# Revit family: Sanitary_Shower-Trays_Sanindusa_Marina-Shower-Tray-With-Schist-Texture-Surface
name_source: partatom
category: Plumbing Fixtures
revit_build: Autodesk Revit 2018 (Build: 20170223_1515(x64)
units: mm (PartAtom-declared; Revit-internal decimal feet)

## family parameters
Always vertical = Yes
Cut with Voids When Loaded = No
OmniClass Number = 23.45.00.00
OmniClass Title = Sanitary, Laundry, and Cleaning Equipment
Part Type = Normal
Room Calculation Point = No
Round Connector Dimension = Use Diameter
Shared = No
Work Plane-Based = No

## types (1)
- Sanitary_Shower-Trays_Sanindusa_Marina-Shower-Tray-With-Schist-Texture-Surface
    AssetType = Fixed
    Color = white
    Constituents = 45111-90 shower tray drain (not included)
    Cost = 0 $
    Description = Installation or waste water appliance that emits a spray of water to wash the human body (BS6100)
    DrainSize = 90 mm  [stored 0.295276 ft]
    Edition number = 1
    Element Type = SHOWER: Installation or waste water appliance that emits a spray of water to wash the human body (BS6100)
    Features = Extra flat shower tray that allows easy accessibility to the shower area. 
Anti-slip finishing, which increases the independence, safety
and comfort in the showers area, especially for children, older people
and people with disability or reduced mobility. Versatile application and contemporary design, also available in colors black or beije. Stonit it is a high-quality inorganic material, suitable for the production of weather-resistant products, similar to natural stone.
    Finish = matte
    Installation Instructions = https://www.tec.sanindusa.pt
    InstallationDate = 1900-12-31T23:59:59
    ManufacturerName = Sanindusa
    ManufacturerURL = www.tec.sanindusa.pt
    Material = Stonit
    ModelNumber = 9516008010
    ModelReference = Marina
    Name = 160x80 marina shower tray with schist texture surface
    NominalHeight = 27 mm  [stored 0.0885827 ft]
    NominalLength = 1600 mm  [stored 5.24934 ft]
    NominalWidth = 800 mm  [stored 2.62467 ft]
    Pre-defined type (IFC) = SHOWER
    Product Guid = 22afca20-d822-447a-a170-03b831770970
    Product data url = https://bimobject.com
    ProductInformation = https://www.tec.sanindusa.pt
    ProductionYear = 2018
    Shape = rectangular
    Size = 160x80
    Type (IFC) = IfcSanitaryTerminalType
    URL = www.tec.sanindusa.pt
    Uniclass2015Code = Pr_40_20_06_84
    Uniclass2015Title = Shower trays
    Uniclass2015Version = Products v1.6
    Version = 1
    WarrantyDescription = https://www.tec.sanindusa.pt
    WarrantyDurationParts = 5
    WarrantyDurationUnit = year
    WarrantyStartDate = 1900-12-31T23:59:59
1900-12-31T23:59:59
    Weight = 27.00 kg

note: [stored X ft] marks values corroborated as IEEE doubles in the binary element streams (Revit-internal decimal feet)

## geometry (parser evidence)
native form markers: Sweep x6
no freeform markers — native parametric forms only
